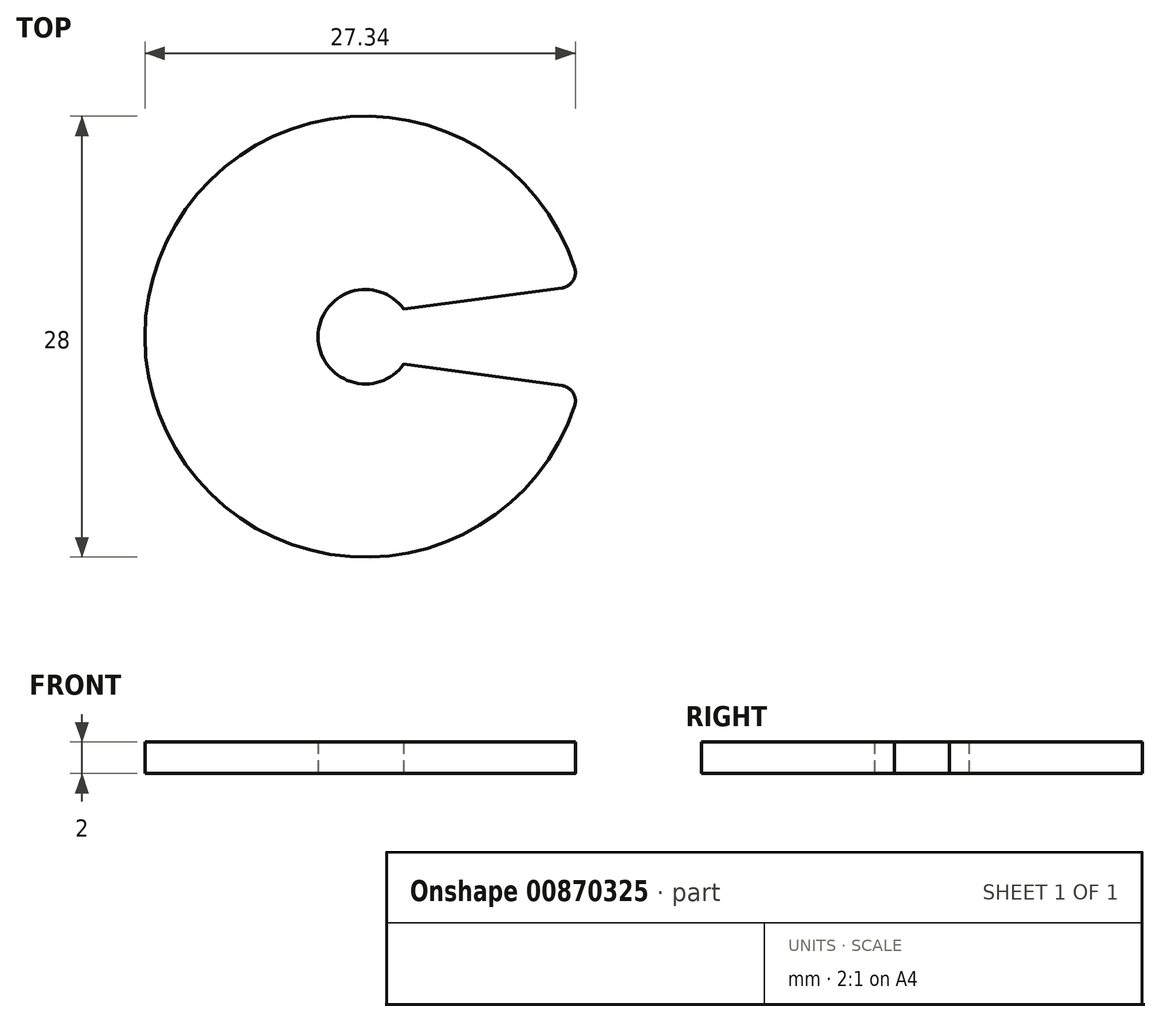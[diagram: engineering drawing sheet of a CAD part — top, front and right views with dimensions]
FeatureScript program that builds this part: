
annotation { "Feature Type Name" : "Feature", "Feature Type Description" : "" }
export const myFeature = defineFeature(function(context is Context, id is Id, definition is map)
    precondition{}
    {
        {
            var Q0;
            Q0=qCreatedBy(makeId("Top.planeOp"),FACE);
            var sketch = newSketch(context, id + "F0", { "sketchPlane" : qUnion([Q0])});
            skArc(sketch, "E0", {"start": v(13.62, -3.25) * mm, "mid": v(-14, 0) * mm, "end": v(13.62, 3.25) * mm});
            skArc(sketch, "E1", {"start": v(2.44, -1.75) * mm, "mid": v(-3, 0) * mm, "end": v(2.44, 1.75) * mm});
            skLineSegment(sketch, "E2", {"start": v(2.44, 1.75) * mm, "end": v(13.62, 3.25) * mm});
            skLineSegment(sketch, "E3", {"start": v(2.44, -1.75) * mm, "end": v(13.62, -3.25) * mm});
            skSolve(sketch);
        }
        {
            var Q0;
            Q0 = qSketchRegion(id + "F0", true);
            extrude(context, id + "F1", {"entities" : qUnion([Q0]), "depth" : 2 * mm, "offsetDistance" : 25 * mm});
        }
        {
            var Q0;
            Q0=makeQuery(id+"F1.opExtrude","SWEPT_EDGE",EDGE,{"disambiguationData":[OSD([sQuery(id+"F0.wireOp",EDGE,"E0"),sQuery(id+"F0.wireOp",EDGE,"E2")])]});
            var Q1;
            Q1=makeQuery(id+"F1.opExtrude","SWEPT_EDGE",EDGE,{"disambiguationData":[OSD([sQuery(id+"F0.wireOp",EDGE,"E0"),sQuery(id+"F0.wireOp",EDGE,"E3")])]});
            fillet(context, id + "F2", {"entities" : qUnion([Q0, Q1]), "radius" : 1 * mm, "tangentPropagation" : true, "allowEdgeOverflow" : false});
        }
    });
